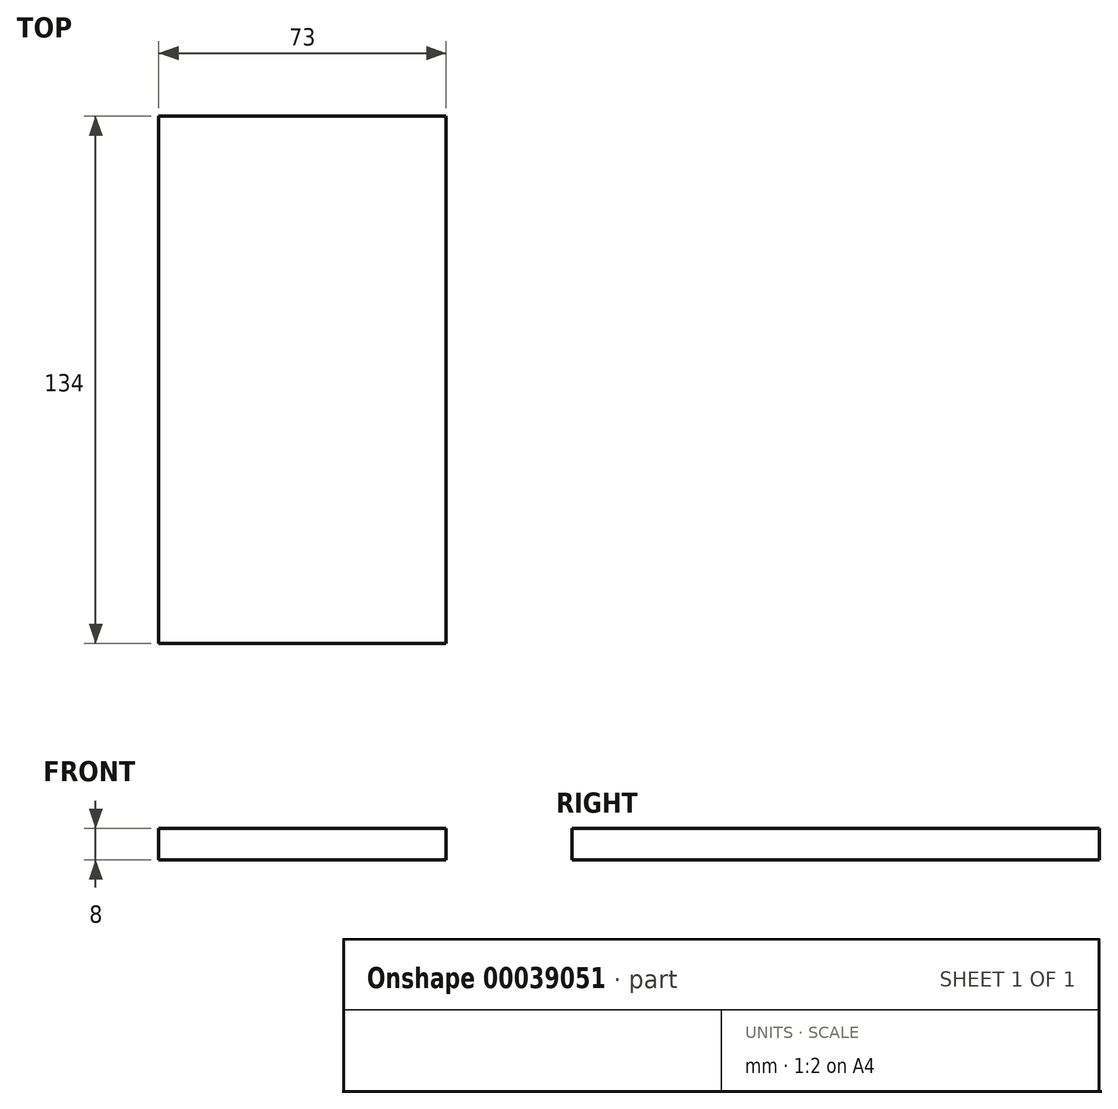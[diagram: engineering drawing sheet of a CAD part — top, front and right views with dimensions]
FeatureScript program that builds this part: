
annotation { "Feature Type Name" : "Feature", "Feature Type Description" : "" }
export const myFeature = defineFeature(function(context is Context, id is Id, definition is map)
    precondition{}
    {
        {
            var Q0;
            Q0=qCreatedBy(makeId("Front.planeOp"),FACE);
            var sketch = newSketch(context, id + "F0", { "sketchPlane" : qUnion([Q0])});
            skLineSegment(sketch, "E0.bottom", {"start": v(0, 0) * mm, "end": v(-73, 0) * mm});
            skLineSegment(sketch, "E0.top", {"start": v(0, -8) * mm, "end": v(-73, -8) * mm});
            skLineSegment(sketch, "E0.left", {"start": v(0, 0) * mm, "end": v(0, -8) * mm});
            skLineSegment(sketch, "E0.right", {"start": v(-73, 0) * mm, "end": v(-73, -8) * mm});
            skSolve(sketch);
        }
        {
            var Q0;
            Q0 = qSketchRegion(id + "F0", true);
            extrude(context, id + "F1", {"entities" : qUnion([Q0]), "depth" : 134 * mm});
        }
    });
